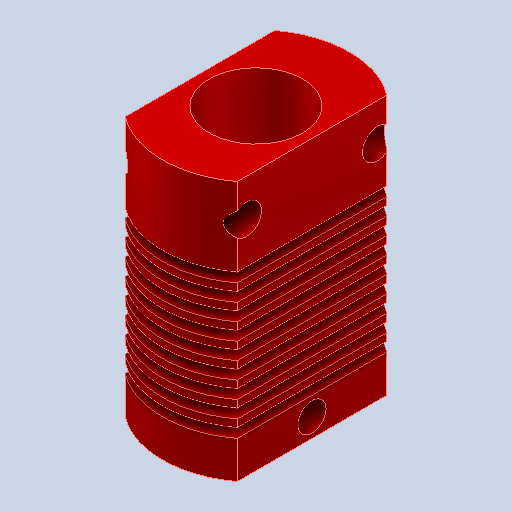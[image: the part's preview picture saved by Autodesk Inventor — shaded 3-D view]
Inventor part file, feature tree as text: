
AUTODESK INVENTOR PART (.ipt)
format: ipt  version: 2022 (Build 260153070, 153G)  size: 303,104 bytes
history: native  units: mm
features: extrude x8, sketch x6, plane x1, pattern_linear x1
ambient origin geometry x8: Origin, YZ Plane, XZ Plane, XY Plane, X Axis, Y Axis, Z Axis, Center Point
bodies: Solid1 (feature_tree)
feature tree (16):
  sketch  "Sketch1"  dims[d0=10.0mm d1=10.0mm]
  extrude  "Extrusion1"  Depth=10.0mm
  plane  "Work Plane1"
  extrude  "Extrusion2"  Depth=3.0mm
  pattern_linear  "Rectangular Pattern1"  Spacing1=-4.0mm  [1 undecoded]
  extrude  "Extrusion3"  Depth=10.0mm TaperAngle=0.0deg
  extrude  "Extrusion4"  Depth=10.0mm
  extrude  "Extrusion5"  Depth=10.0mm
  extrude  "Extrusion6"  Depth=10.0mm TaperAngle=0.0deg
  extrude  "Extrusion7"  Depth=10.0mm
  extrude  "Extrusion8"  Depth=10.0mm TaperAngle=0.0deg
  sketch  "Sketch2"  dims[d3=12.0mm d4=3.0mm]
  sketch  "Sketch3"  dims[d5=7.0mm]
  sketch  "Sketch4"  dims[d6=1.5mm]
  sketch  "Sketch5"  dims[d7=7.0mm]
  sketch  "Sketch6"  dims[d8=27.8mm d9=0.0mm d10=-4.0mm d11=1.0mm d12=0.0mm d13=90.0mm d15=1.8mm d16=8.6mm d17=16.7mm d18=0.0mm d19=6.0mm d20=3.1mm d21=0.0mm d22=10.0mm d23=8.0mm d24=0.0mm d25=4.0mm d26=0.0mm d27=3.2mm d28=23.8mm d29=14.0mm d31=7.0mm d32=12.0mm d33=0.0mm d34=2.0mm d35=3.0mm d36=4.75mm d37=0.0mm]
note: 1 required parameter value undecoded (feature->parameter linkage not recoverable at this tier; creation-order binding heuristic only, values carry confidence <= 0.55)
